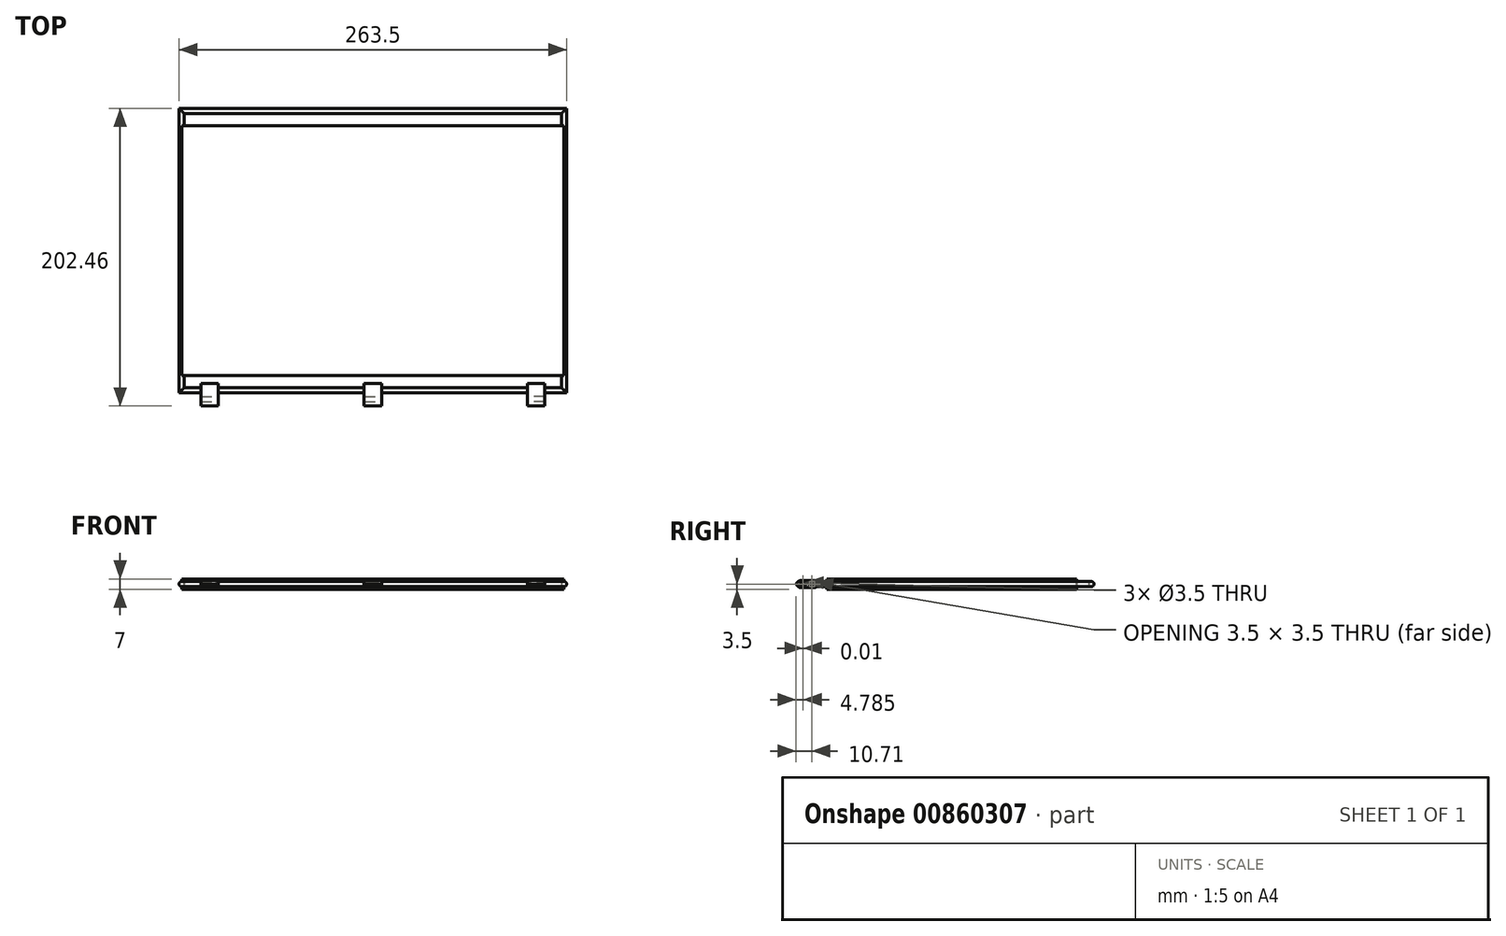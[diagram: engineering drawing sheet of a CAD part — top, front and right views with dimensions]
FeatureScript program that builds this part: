
annotation { "Feature Type Name" : "Feature", "Feature Type Description" : "" }
export const myFeature = defineFeature(function(context is Context, id is Id, definition is map)
    precondition{}
    {
        {
            var Q0;
            Q0=qCreatedBy(makeId("Top.planeOp"),FACE);
            var sketch = newSketch(context, id + "F0", { "sketchPlane" : qUnion([Q0])});
            skLineSegment(sketch, "E0", {"start": v(-130, 85) * mm, "end": v(130, 85) * mm});
            skLineSegment(sketch, "E1", {"start": v(-130, -85) * mm, "end": v(130, -85) * mm});
            skLineSegment(sketch, "E2", {"start": v(-130, 85) * mm, "end": v(-130, -85) * mm});
            skLineSegment(sketch, "E3", {"start": v(130, 85) * mm, "end": v(130, -85) * mm});
            skLineSegment(sketch, "E4", {"start": v(-130, 85) * mm, "end": v(-130, 95) * mm});
            skLineSegment(sketch, "E5", {"start": v(-130, 95) * mm, "end": v(130, 95) * mm});
            skLineSegment(sketch, "E6", {"start": v(130, 85) * mm, "end": v(130, 95) * mm});
            skLineSegment(sketch, "E7", {"start": v(-130, -85) * mm, "end": v(-130, -95) * mm});
            skLineSegment(sketch, "E8", {"start": v(-130, -95) * mm, "end": v(130, -95) * mm});
            skLineSegment(sketch, "E9", {"start": v(130, -95) * mm, "end": v(130, -85) * mm});
            skLineSegment(sketch, "E10", {"start": v(-110.97, -86.9) * mm, "end": v(-110.97, -107.59) * mm});
            skLineSegment(sketch, "E11.bottom", {"start": v(-116.97, -90) * mm, "end": v(-104.97, -90) * mm});
            skLineSegment(sketch, "E11.top", {"start": v(-116.97, -106) * mm, "end": v(-104.97, -106) * mm});
            skLineSegment(sketch, "E11.left", {"start": v(-116.97, -90) * mm, "end": v(-116.97, -106) * mm});
            skLineSegment(sketch, "E11.right", {"start": v(-104.97, -90) * mm, "end": v(-104.97, -106) * mm});
            skLineSegment(sketch, "E12", {"start": v(0, 85) * mm, "end": v(0, -137.84) * mm});
            skLineSegment(sketch, "E13.bottom", {"start": v(-6, -106) * mm, "end": v(6, -106) * mm});
            skLineSegment(sketch, "E13.top", {"start": v(-6, -90) * mm, "end": v(6, -90) * mm});
            skLineSegment(sketch, "E13.left", {"start": v(-6, -106) * mm, "end": v(-6, -90) * mm});
            skLineSegment(sketch, "E13.right", {"start": v(6, -106) * mm, "end": v(6, -90) * mm});
            skSolve(sketch);
        }
        {
            var Q0;
            Q0=makeQuery(id+"F0.imprint","IMPRINT",FACE,{"disambiguationData":[TD([[makeQuery(id+"F0.imprint","IMPRINT",EDGE,{"derivedFrom":sQuery(id+"F0.wireOp",EDGE,"E0")}),-1.0]])]});
            extrude(context, id + "F1", {"entities" : qUnion([Q0]), "endBound" : BoundingType.SYMMETRIC, "oppositeDirection" : true, "depth" : 7 * mm, "offsetDistance" : 25 * mm});
        }
        {
            var Q0;
            Q0=qCreatedBy(makeId("Front.planeOp"),FACE);
            cPlane(context, id + "F2", {"entities" : qUnion([Q0]), "cplaneType" : CPlaneType.OFFSET, "offset" : 95 * mm, "oppositeDirection" : true, "width" : 150 * mm, "height" : 150 * mm});
        }
        {
            var Q0;
            Q0=qCreatedBy(id+"F2.planeOp",FACE);
            var sketch = newSketch(context, id + "F3", { "sketchPlane" : qUnion([Q0])});
            skCircle(sketch, "E14", {"center": v(130, 0) * mm, "radius": 1.75 * mm});
            skSolve(sketch);
        }
        {
            var Q0;
            Q0=makeQuery(id+"F3.imprint","IMPRINT",FACE,{"disambiguationData":[TD([[makeQuery(id+"F3.imprint","IMPRINT",EDGE,{"derivedFrom":sQuery(id+"F3.wireOp",EDGE,"E14")}),1.0]])]});
            var Q1;
            Q1=sQuery(id+"F0.wireOp",EDGE,"E6");
            var Q2;
            Q2=sQuery(id+"F0.wireOp",EDGE,"E3");
            var Q3;
            Q3=sQuery(id+"F0.wireOp",EDGE,"E5");
            var Q4;
            Q4=sQuery(id+"F0.wireOp",EDGE,"E4");
            var Q5;
            Q5=sQuery(id+"F0.wireOp",EDGE,"E2");
            var Q6;
            Q6=sQuery(id+"F0.wireOp",EDGE,"E7");
            var Q7;
            Q7=sQuery(id+"F0.wireOp",EDGE,"E8");
            var Q8;
            Q8=sQuery(id+"F0.wireOp",EDGE,"E9");
            sweep(context, id + "F4", {"operationType" : NewBodyOperationType.ADD, "profiles" : qUnion([Q0]), "path" : qUnion([Q1, Q2, Q3, Q4, Q5, Q6, Q7, Q8])});
        }
        {
            var Q0;
            {var subQ1=sQuery(id+"F0.wireOp",EDGE,"E11.top");Q0=makeQuery(id+"F0.imprint","IMPRINT",FACE,{"disambiguationData":[TD([[makeQuery(id+"F0.imprint","IMPRINT",EDGE,{"derivedFrom":subQ1}),1.0]])]});}
            var Q1;
            {var subQ0=sQuery(id+"F0.wireOp",EDGE,"E10");var subQ1=sQuery(id+"F0.wireOp",EDGE,"E8");var subQ2=makeQuery(id+"F0.imprint","INTERSECT",VERTEX,{"derivedFrom":[subQ1,subQ0]});Q1=makeQuery(id+"F0.imprint","IMPRINT",FACE,{"disambiguationData":[TD([[makeQuery(id+"F0.imprint","IMPRINT",EDGE,{"disambiguationData":[TD([[subQ2,-1.0]])],"derivedFrom":subQ1}),1.0]])]});}
            var Q2;
            {var subQ0=sQuery(id+"F0.wireOp",EDGE,"E11.left");var subQ1=sQuery(id+"F0.wireOp",EDGE,"E8");var subQ2=makeQuery(id+"F0.imprint","INTERSECT",VERTEX,{"derivedFrom":[subQ1,subQ0]});Q2=makeQuery(id+"F0.imprint","IMPRINT",FACE,{"disambiguationData":[TD([[makeQuery(id+"F0.imprint","IMPRINT",EDGE,{"disambiguationData":[TD([[subQ2,-1.0]])],"derivedFrom":subQ1}),1.0]])]});}
            extrude(context, id + "F5", {"entities" : qUnion([Q0, Q1, Q2]), "operationType" : NewBodyOperationType.ADD, "endBound" : BoundingType.SYMMETRIC, "depth" : 5 * mm, "offsetDistance" : 25 * mm});
        }
        {
            var Q0;
            Q0=makeQuery(id+"F5.opExtrude","CAP_EDGE",EDGE,{"disambiguationData":[OSD([sQuery(id+"F0.wireOp",EDGE,"E11.top")])],"isStart":false});
            var Q1;
            Q1=makeQuery(id+"F5.opExtrude","CAP_EDGE",EDGE,{"disambiguationData":[OSD([sQuery(id+"F0.wireOp",EDGE,"E11.top")])],"isStart":true});
            var Q2;
            Q2=makeQuery(id+"F5.opExtrude","CAP_EDGE",EDGE,{"disambiguationData":[OSD([sQuery(id+"F0.wireOp",EDGE,"E11.bottom")])],"isStart":false});
            var Q3;
            Q3=makeQuery(id+"F5.opExtrude","CAP_EDGE",EDGE,{"disambiguationData":[OSD([sQuery(id+"F0.wireOp",EDGE,"E11.bottom")])],"isStart":true});
            fillet(context, id + "F6", {"entities" : qUnion([Q0, Q1, Q2, Q3]), "radius" : 4 * mm, "tangentPropagation" : true, "allowEdgeOverflow" : false});
        }
        {
            var Q0;
            Q0=makeQuery(id+"F5.opExtrude","SWEPT_FACE",FACE,{"disambiguationData":[OSD([sQuery(id+"F0.wireOp",EDGE,"E11.right")])]});
            cPlane(context, id + "F7", {"entities" : qUnion([Q0]), "cplaneType" : CPlaneType.OFFSET, "offset" : 0 * mm, "oppositeDirection" : true, "width" : 150 * mm, "height" : 150 * mm});
        }
        {
            var Q0;
            Q0=qCreatedBy(id+"F7.planeOp",FACE);
            var sketch = newSketch(context, id + "F8", { "sketchPlane" : qUnion([Q0])});
            skCircle(sketch, "E15", {"center": v(-100.91, 0) * mm, "radius": 1.75 * mm});
            skSolve(sketch);
        }
        {
            var Q0;
            Q0=makeQuery(id+"F8.imprint","IMPRINT",FACE,{"disambiguationData":[TD([[makeQuery(id+"F8.imprint","IMPRINT",EDGE,{"derivedFrom":sQuery(id+"F8.wireOp",EDGE,"E15")}),1.0]])]});
            extrude(context, id + "F9", {"entities" : qUnion([Q0]), "operationType" : NewBodyOperationType.REMOVE, "endBound" : BoundingType.UP_TO_NEXT, "oppositeDirection" : true, "depth" : 25 * mm, "offsetDistance" : 25 * mm});
        }
        {
            var Q0;
            Q0=makeQuery(id+"F1.opExtrude","SWEPT_BODY",BODY,{"disambiguationData":[OSD([sQuery(id+"F0.wireOp",EDGE,"E0"),sQuery(id+"F0.wireOp",EDGE,"E1"),sQuery(id+"F0.wireOp",EDGE,"E2"),sQuery(id+"F0.wireOp",EDGE,"E3")])]});
            var Q1;
            Q1=qCreatedBy(makeId("Right.planeOp"),FACE);
            mirror(context, id + "F10", {"operationType" : NewBodyOperationType.ADD, "entities" : qUnion([Q0]), "mirrorPlane" : qUnion([Q1])});
        }
        {
            var Q0;
            {var subQ0=sQuery(id+"F0.wireOp",EDGE,"E13.left");var subQ1=sQuery(id+"F0.wireOp",EDGE,"E8");var subQ2=makeQuery(id+"F0.imprint","INTERSECT",VERTEX,{"derivedFrom":[subQ1,subQ0]});Q0=makeQuery(id+"F0.imprint","IMPRINT",FACE,{"disambiguationData":[TD([[makeQuery(id+"F0.imprint","IMPRINT",EDGE,{"disambiguationData":[TD([[subQ2,-1.0]])],"derivedFrom":subQ1}),-1.0]])]});}
            var Q1;
            {var subQ0=sQuery(id+"F0.wireOp",EDGE,"E13.left");var subQ1=sQuery(id+"F0.wireOp",EDGE,"E8");var subQ2=makeQuery(id+"F0.imprint","INTERSECT",VERTEX,{"derivedFrom":[subQ1,subQ0]});Q1=makeQuery(id+"F0.imprint","IMPRINT",FACE,{"disambiguationData":[TD([[makeQuery(id+"F0.imprint","IMPRINT",EDGE,{"disambiguationData":[TD([[subQ2,-1.0]])],"derivedFrom":subQ1}),1.0]])]});}
            var Q2;
            {var subQ0=sQuery(id+"F0.wireOp",EDGE,"E13.right");var subQ1=sQuery(id+"F0.wireOp",EDGE,"E8");var subQ2=makeQuery(id+"F0.imprint","INTERSECT",VERTEX,{"derivedFrom":[subQ1,subQ0]});Q2=makeQuery(id+"F0.imprint","IMPRINT",FACE,{"disambiguationData":[TD([[makeQuery(id+"F0.imprint","IMPRINT",EDGE,{"disambiguationData":[TD([[subQ2,1.0]])],"derivedFrom":subQ1}),1.0]])]});}
            var Q3;
            {var subQ0=sQuery(id+"F0.wireOp",EDGE,"E13.right");var subQ1=sQuery(id+"F0.wireOp",EDGE,"E8");var subQ2=makeQuery(id+"F0.imprint","INTERSECT",VERTEX,{"derivedFrom":[subQ1,subQ0]});Q3=makeQuery(id+"F0.imprint","IMPRINT",FACE,{"disambiguationData":[TD([[makeQuery(id+"F0.imprint","IMPRINT",EDGE,{"disambiguationData":[TD([[subQ2,1.0]])],"derivedFrom":subQ1}),-1.0]])]});}
            extrude(context, id + "F11", {"entities" : qUnion([Q0, Q1, Q2, Q3]), "operationType" : NewBodyOperationType.ADD, "endBound" : BoundingType.SYMMETRIC, "depth" : 5 * mm, "offsetDistance" : 25 * mm});
        }
        {
            var Q0;
            Q0=makeQuery(id+"F11.opExtrude","CAP_EDGE",EDGE,{"disambiguationData":[OSD([sQuery(id+"F0.wireOp",EDGE,"E13.bottom")])],"isStart":false});
            var Q1;
            Q1=makeQuery(id+"F11.opExtrude","CAP_EDGE",EDGE,{"disambiguationData":[OSD([sQuery(id+"F0.wireOp",EDGE,"E13.top")])],"isStart":false});
            var Q2;
            Q2=makeQuery(id+"F11.opExtrude","CAP_EDGE",EDGE,{"disambiguationData":[OSD([sQuery(id+"F0.wireOp",EDGE,"E13.bottom")])],"isStart":true});
            var Q3;
            Q3=makeQuery(id+"F11.opExtrude","CAP_EDGE",EDGE,{"disambiguationData":[OSD([sQuery(id+"F0.wireOp",EDGE,"E13.top")])],"isStart":true});
            fillet(context, id + "F12", {"entities" : qUnion([Q0, Q1, Q2, Q3]), "radius" : 4 * mm, "tangentPropagation" : true, "allowEdgeOverflow" : false});
        }
        {
            var Q0;
            Q0=makeQuery(id+"F11.opExtrude","SWEPT_FACE",FACE,{"disambiguationData":[OSD([sQuery(id+"F0.wireOp",EDGE,"E13.right")])]});
            cPlane(context, id + "F13", {"entities" : qUnion([Q0]), "cplaneType" : CPlaneType.OFFSET, "offset" : 0 * mm, "width" : 150 * mm, "height" : 150 * mm});
        }
        {
            var Q0;
            Q0=qCreatedBy(id+"F13.planeOp",FACE);
            var sketch = newSketch(context, id + "F14", { "sketchPlane" : qUnion([Q0])});
            skCircle(sketch, "E16", {"center": v(-100.92, 0) * mm, "radius": 1.75 * mm});
            skLineSegment(sketch, "E17", {"start": v(-95, 0) * mm, "end": v(-100.92, 0) * mm});
            skLineSegment(sketch, "E18", {"start": v(-100.31, 0.38) * mm, "end": v(-99.44, 0.93) * mm});
            skSolve(sketch);
        }
        {
            var Q0;
            {var subQ0=sQuery(id+"F14.wireOp",EDGE,"E16");Q0=makeQuery(id+"F14.imprint","IMPRINT",FACE,{"disambiguationData":[TD([[makeQuery(id+"F14.imprint","IMPRINT",EDGE,{"disambiguationData":[TD([[makeQuery(id+"F14.imprint","IMPRINT",VERTEX,{"derivedFrom":subQ0}),-1.0]])],"derivedFrom":subQ0}),1.0]])]});}
            extrude(context, id + "F15", {"entities" : qUnion([Q0]), "operationType" : NewBodyOperationType.REMOVE, "endBound" : BoundingType.UP_TO_NEXT, "oppositeDirection" : true, "depth" : 25 * mm, "offsetDistance" : 25 * mm});
        }
    });
